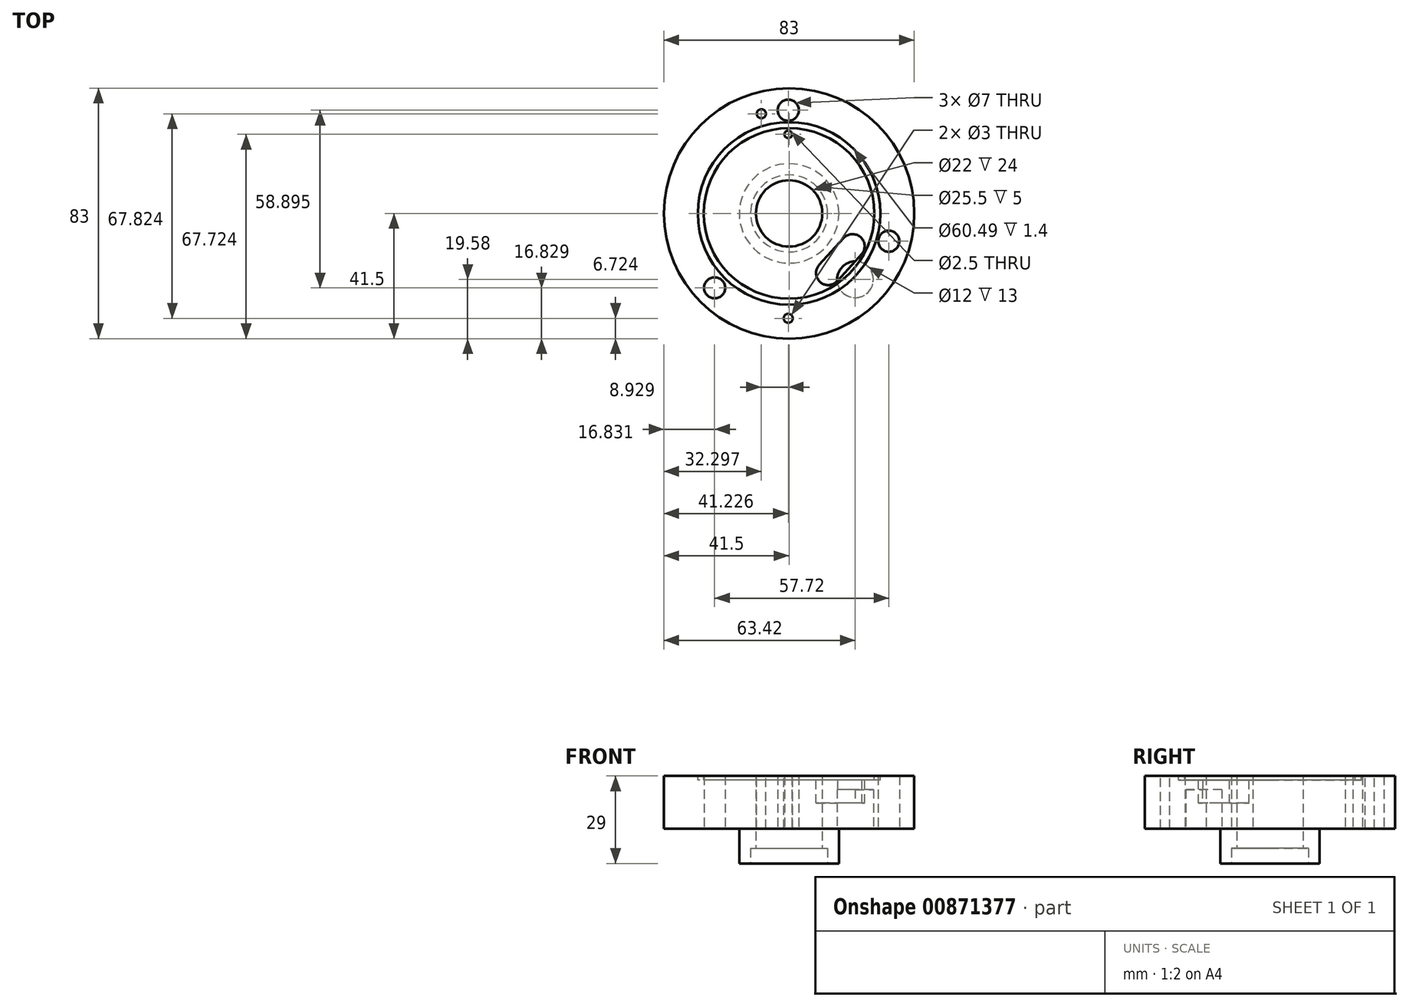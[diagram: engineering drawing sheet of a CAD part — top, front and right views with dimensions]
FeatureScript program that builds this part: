
annotation { "Feature Type Name" : "Feature", "Feature Type Description" : "" }
export const myFeature = defineFeature(function(context is Context, id is Id, definition is map)
    precondition{}
    {
        {
            var Q0;
            Q0=qCreatedBy(makeId("Top.planeOp"),FACE);
            var sketch = newSketch(context, id + "F0", { "sketchPlane" : qUnion([Q0])});
            skCircle(sketch, "E0", {"center": v(0, 0) * mm, "radius": 41.5 * mm});
            skSolve(sketch);
        }
        {
            var Q0;
            Q0 = qSketchRegion(id + "F0", true);
            extrude(context, id + "F1", {"entities" : qUnion([Q0]), "depth" : 29 * mm, "offsetDistance" : 25 * mm});
        }
        {
            var Q0;
            Q0=makeQuery(id+"F1.opExtrude","CAP_FACE",FACE,{"disambiguationData":[OSD([sQuery(id+"F0.wireOp",EDGE,"E0")])],"isStart":true});
            var sketch = newSketch(context, id + "F2", { "sketchPlane" : qUnion([Q0])});
            skCircle(sketch, "E1", {"center": v(0, 0) * mm, "radius": 16.5 * mm});
            skSolve(sketch);
        }
        {
            var Q0;
            Q0=makeQuery(id+"F2.imprint","IMPRINT",FACE,{"disambiguationData":[TD([[makeQuery(id+"F2.imprint","IMPRINT",EDGE,{"derivedFrom":sQuery(id+"F2.wireOp",EDGE,"E1")}),-1.0]])]});
            extrude(context, id + "F3", {"entities" : qUnion([Q0]), "operationType" : NewBodyOperationType.REMOVE, "oppositeDirection" : true, "depth" : 11.5 * mm, "offsetDistance" : 25 * mm});
        }
        {
            var Q0;
            Q0=makeQuery(id+"F1.opExtrude","CAP_FACE",FACE,{"disambiguationData":[OSD([sQuery(id+"F0.wireOp",EDGE,"E0")])],"isStart":true});
            var sketch = newSketch(context, id + "F4", { "sketchPlane" : qUnion([Q0])});
            skCircle(sketch, "E2", {"center": v(0, 0) * mm, "radius": 11 * mm});
            skSolve(sketch);
        }
        {
            var Q0;
            Q0 = qSketchRegion(id + "F4", true);
            extrude(context, id + "F5", {"entities" : qUnion([Q0]), "operationType" : NewBodyOperationType.REMOVE, "endBound" : BoundingType.THROUGH_ALL, "oppositeDirection" : true, "depth" : 25 * mm, "offsetDistance" : 25 * mm});
        }
        {
            var Q0;
            Q0=makeQuery(id+"F1.opExtrude","CAP_FACE",FACE,{"disambiguationData":[OSD([sQuery(id+"F0.wireOp",EDGE,"E0")])],"isStart":true});
            var sketch = newSketch(context, id + "F6", { "sketchPlane" : qUnion([Q0])});
            skCircle(sketch, "E3", {"center": v(0, 0) * mm, "radius": 12.75 * mm});
            skSolve(sketch);
        }
        {
            var Q0;
            Q0 = qSketchRegion(id + "F6", true);
            extrude(context, id + "F7", {"entities" : qUnion([Q0]), "operationType" : NewBodyOperationType.REMOVE, "oppositeDirection" : true, "depth" : 5 * mm, "offsetDistance" : 25 * mm});
        }
        {
            var Q0;
            Q0=makeQuery(id+"F1.opExtrude","CAP_FACE",FACE,{"disambiguationData":[OSD([sQuery(id+"F0.wireOp",EDGE,"E0")])],"isStart":false});
            var sketch = newSketch(context, id + "F8", { "sketchPlane" : qUnion([Q0])});
            skPoint(sketch, "E4", {"position": v(0, 0) * mm});
            skPoint(sketch, "E5", {"position": v(-0.27, 34.22) * mm});
            skPoint(sketch, "E6", {"position": v(-0.27, 26.22) * mm});
            skPoint(sketch, "E7", {"position": v(-0.27, -34.78) * mm});
            skPoint(sketch, "E8", {"position": v(-9.2, 33.05) * mm});
            skPoint(sketch, "E9", {"position": v(-18.02, 30.47) * mm});
            skPoint(sketch, "E10", {"position": v(-24.67, -24.67) * mm});
            skPoint(sketch, "E11", {"position": v(17.48, -31.02) * mm});
            skPoint(sketch, "E12", {"position": v(33.05, -9.2) * mm});
            skCircle(sketch, "E13", {"center": v(-9.2, 33.05) * mm, "radius": 1.5 * mm});
            skCircle(sketch, "E14", {"center": v(-0.27, -34.78) * mm, "radius": 1.5 * mm});
            skLineSegment(sketch, "E15", {"start": v(-0.27, -0.28) * mm, "end": v(-0.27, 44.82) * mm, "construction": true});
            skLineSegment(sketch, "E16", {"start": v(-0.27, -0.28) * mm, "end": v(33.05, -9.2) * mm, "construction": true});
            skSolve(sketch);
        }
        {
            var Q0;
            Q0=makeQuery(id+"F8.imprint","IMPRINT",FACE,{"disambiguationData":[TD([[makeQuery(id+"F8.imprint","IMPRINT",EDGE,{"derivedFrom":sQuery(id+"F8.wireOp",EDGE,"E13")}),1.0]])]});
            var Q1;
            Q1=makeQuery(id+"F8.imprint","IMPRINT",FACE,{"disambiguationData":[TD([[makeQuery(id+"F8.imprint","IMPRINT",EDGE,{"derivedFrom":sQuery(id+"F8.wireOp",EDGE,"E14")}),1.0]])]});
            extrude(context, id + "F9", {"entities" : qUnion([Q0, Q1]), "operationType" : NewBodyOperationType.REMOVE, "endBound" : BoundingType.THROUGH_ALL, "oppositeDirection" : true, "depth" : 25 * mm, "offsetDistance" : 25 * mm});
        }
        {
            var Q0;
            Q0=sQuery(id+"F8.wireOp",VERTEX,"E5");
            var Q1;
            Q1=sQuery(id+"F8.wireOp",VERTEX,"E12");
            var Q2;
            Q2=sQuery(id+"F8.wireOp",VERTEX,"E10");
            var Q3;
            Q3=makeQuery(id+"F1.opExtrude","SWEPT_BODY",BODY,{"disambiguationData":[OSD([sQuery(id+"F0.wireOp",EDGE,"E0")])]});
            hole(context, id + "F10", {"style" : HoleStyle.SIMPLE, "endStyle" : HoleEndStyle.THROUGH, "holeDiameter" : 7 * mm, "majorDiameter" : 5 * mm, "isTappedThrough" : true, "tappedDepth" : 12 * mm, "tapClearance" : 3, "locations" : qUnion([Q0, Q1, Q2]), "scope" : qUnion([Q3]), "startStyle" : HoleStartStyle.SKETCH});
        }
        {
            var Q0;
            Q0=qCreatedBy(makeId("Front.planeOp"),FACE);
            var sketch = newSketch(context, id + "F11", { "sketchPlane" : qUnion([Q0])});
            skLineSegment(sketch, "E17.bottom", {"start": v(28.24, 29) * mm, "end": v(30.24, 29) * mm});
            skLineSegment(sketch, "E17.top", {"start": v(28.24, 27.6) * mm, "end": v(30.24, 27.6) * mm});
            skLineSegment(sketch, "E17.left", {"start": v(28.24, 29) * mm, "end": v(28.24, 27.6) * mm});
            skLineSegment(sketch, "E17.right", {"start": v(30.24, 29) * mm, "end": v(30.24, 27.6) * mm});
            skLineSegment(sketch, "E18", {"start": v(0, -18.6) * mm, "end": v(0, 42) * mm, "construction": true});
            skSolve(sketch);
        }
        {
            var Q0;
            Q0 = qSketchRegion(id + "F11", true);
            var Q1;
            Q1=sQuery(id+"F11.wireOp",EDGE,"E18");
            revolve(context, id + "F12", {"operationType" : NewBodyOperationType.REMOVE, "surfaceOperationType" : NewSurfaceOperationType.NEW, "entities" : qUnion([Q0]), "axis" : qUnion([Q1]), "revolveType" : RevolveType.FULL, "oppositeDirection" : true});
        }
        {
            var Q0;
            Q0=sQuery(id+"F8.wireOp",VERTEX,"E6");
            var Q1;
            Q1=makeQuery(id+"F1.opExtrude","SWEPT_BODY",BODY,{"disambiguationData":[OSD([sQuery(id+"F0.wireOp",EDGE,"E0")])]});
            hole(context, id + "F13", {"style" : HoleStyle.SIMPLE, "endStyle" : HoleEndStyle.THROUGH, "holeDiameter" : 2.5 * mm, "majorDiameter" : 5 * mm, "isTappedThrough" : true, "tappedDepth" : 12 * mm, "tapClearance" : 3, "locations" : qUnion([Q0]), "scope" : qUnion([Q1]), "startStyle" : HoleStartStyle.SKETCH});
        }
        {
            var Q0;
            Q0=makeQuery(id+"F12.boolean.opBoolean","SPLIT",FACE,{"disambiguationData":[TD([makeQuery(id+"F5.boolean.opBoolean","COPY",FACE,{"derivedFrom":makeQuery(id+"F5.opExtrude","SWEPT_FACE",FACE,{"disambiguationData":[OSD([sQuery(id+"F4.wireOp",EDGE,"E2")])]})})])],"derivedFrom":makeQuery(id+"F1.opExtrude","CAP_FACE",FACE,{"disambiguationData":[OSD([sQuery(id+"F0.wireOp",EDGE,"E0")])],"isStart":false})});
            var sketch = newSketch(context, id + "F14", { "sketchPlane" : qUnion([Q0])});
            skLineSegment(sketch, "E19", {"start": v(24.2, -13.35) * mm, "end": v(16.1, -22.21) * mm});
            skLineSegment(sketch, "E20", {"start": v(18.08, -8.18) * mm, "end": v(9.99, -17.05) * mm});
            skArc(sketch, "E21", {"start": v(9.99, -17.05) * mm, "mid": v(10.36, -22.8) * mm, "end": v(16.1, -22.21) * mm});
            skArc(sketch, "E22", {"start": v(24.2, -13.35) * mm, "mid": v(23.62, -7.82) * mm, "end": v(18.08, -8.18) * mm});
            skSolve(sketch);
        }
        {
            var Q0;
            Q0=makeQuery(id+"F14.imprint","IMPRINT",FACE,{"disambiguationData":[TD([[makeQuery(id+"F14.imprint","IMPRINT",EDGE,{"derivedFrom":sQuery(id+"F14.wireOp",EDGE,"E19")}),-1.0]])]});
            extrude(context, id + "F15", {"entities" : qUnion([Q0]), "operationType" : NewBodyOperationType.REMOVE, "oppositeDirection" : true, "depth" : 9 * mm, "offsetDistance" : 25 * mm});
        }
        {
            var Q0;
            Q0=makeQuery(id+"F3.boolean.opBoolean","COPY",FACE,{"derivedFrom":makeQuery(id+"F3.opExtrude","CAP_FACE",FACE,{"disambiguationData":[OSD([sQuery(id+"F0.wireOp",EDGE,"E0"),sQuery(id+"F2.wireOp",EDGE,"E1")])],"isStart":false})});
            var sketch = newSketch(context, id + "F16", { "sketchPlane" : qUnion([Q0])});
            skLineSegment(sketch, "E23", {"start": v(0, 0) * mm, "end": v(35.98, 35.98) * mm, "construction": true});
            skLineSegment(sketch, "E24", {"start": v(35.98, 35.98) * mm, "end": v(0, 0) * mm, "construction": true});
            skLineSegment(sketch, "E25", {"start": v(0, -49.08) * mm, "end": v(0, 0) * mm, "construction": true});
            skPoint(sketch, "E26", {"position": v(21.92, 21.92) * mm});
            skCircle(sketch, "E27", {"center": v(21.92, 21.92) * mm, "radius": 6 * mm});
            skSolve(sketch);
        }
        {
            var Q0;
            Q0 = qSketchRegion(id + "F16", true);
            extrude(context, id + "F17", {"entities" : qUnion([Q0]), "operationType" : NewBodyOperationType.REMOVE, "oppositeDirection" : true, "depth" : 13 * mm, "offsetDistance" : 25 * mm});
        }
    });
